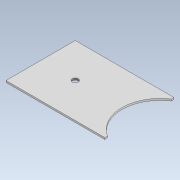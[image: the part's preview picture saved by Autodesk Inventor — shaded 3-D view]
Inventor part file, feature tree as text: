
AUTODESK INVENTOR PART (.ipt)
format: ipt  version: 2021 (Build 250183000, 183)  size: 105,472 bytes
history: native  units: mm
features: sketch x4, extrude x3, other x1, hole x1
ambient origin geometry x8: Origin, YZ Plane, XZ Plane, XY Plane, X Axis, Y Axis, Z Axis, Center Point
bodies: Body1 (feature_tree)
feature tree (9):
  other  "Sólido1"
  extrude  "Extrusión1"  Depth=40.0mm
  extrude  "Extrusión2"  Depth=1.0mm
  extrude  "Extrusión3"  TaperAngle=0.0deg  [1 undecoded]
  hole  "Agujero1"  [1 undecoded]
  sketch  "Boceto1"  dims[d1=60.0mm d3=40.0mm]
  sketch  "Boceto2"  dims[d4=1.0mm d5=0.0mm d7=44.0mm]
  sketch  "Boceto3"  dims[d8=9.0mm d9=0.0mm d10=0.0mm]
  sketch  "Boceto4"  dims[d11=57.0mm d12=0.0mm d13=0.0mm d14=3.4mm d15=6.0mm d16=4.0mm d17=2.0mm d18=90.0deg d19=8.0mm d20=0.0mm]
note: 2 required parameter values undecoded (feature->parameter linkage not recoverable at this tier; creation-order binding heuristic only, values carry confidence <= 0.55)
